# Revit family: Heater-Bromic-Tungsten-Electric-Wall-Mounted2
name_source: partatom
category: Mechanical Equipment
units: mm (PartAtom-declared; Revit-internal decimal feet)

## family parameters
Classification = None
Cut with Voids When Loaded = No
Host = Face
OmniClass Number = 23.75.10.14
OmniClass Title = Independent Electric Heating Units
Part Type = Normal
Room Calculation Point = No
Round Connector Dimension = Use Diameter
Shared = No

## types (1)
- Not a Type - Laod Type Catalog!
    Apparent Load = 2000 VA
    Approximate Heat Area = 65.00 SF
    Default Elevation = 71 "
    Depth = 4 "
    Description = The Tungsten Smart-Heat™ Electric range brings high-performance radiant heating to open outdoor applications and semi-enclosed spaces alike. This heater’s extended body and reflector provides a wide wall of heat across a vast footprint, maximizing the comfort created by each unit. Available in 4 models with heat outputs of up to 6kW, these units emit minimal light and present a scalable solution for those wishing to tailor heating systems specifically to the space serviced.
    End Clearance = 12 "
    Floor Clearance = 72 "
    Head Clearance = 5 "
    Heater Type Selector = 1
    LegInset = 9 "
    Length = 44 "
    Load Classification = Power
    Load Sub-Classification Motor = No
    Manufacturer = Bromic Heating
    Material = Metal-Steel-Bromic-Black
    Model = Tungsten Smart-Heat™ Electric
    Number of Poles = 1
    Power Factor = 1
    Product data url = https://www.bimobject.com
    ProductCode = ProductCode not specified - Load Type Catalog!
    Screen Material = Metal-Steel-Bromic-Black-Perforated
    URL = https://www.bromic.com
    Utility = No
    Voltage = 208 V
    Wattage = 2000 W
    Weight = 19.80 lb
    Width = 9 "
    calcDepth = 3 "
    calcLength = 44 "
    calcWidth = 8 "

## geometry (parser evidence)
native form markers: Sweep x7
no freeform markers — native parametric forms only
